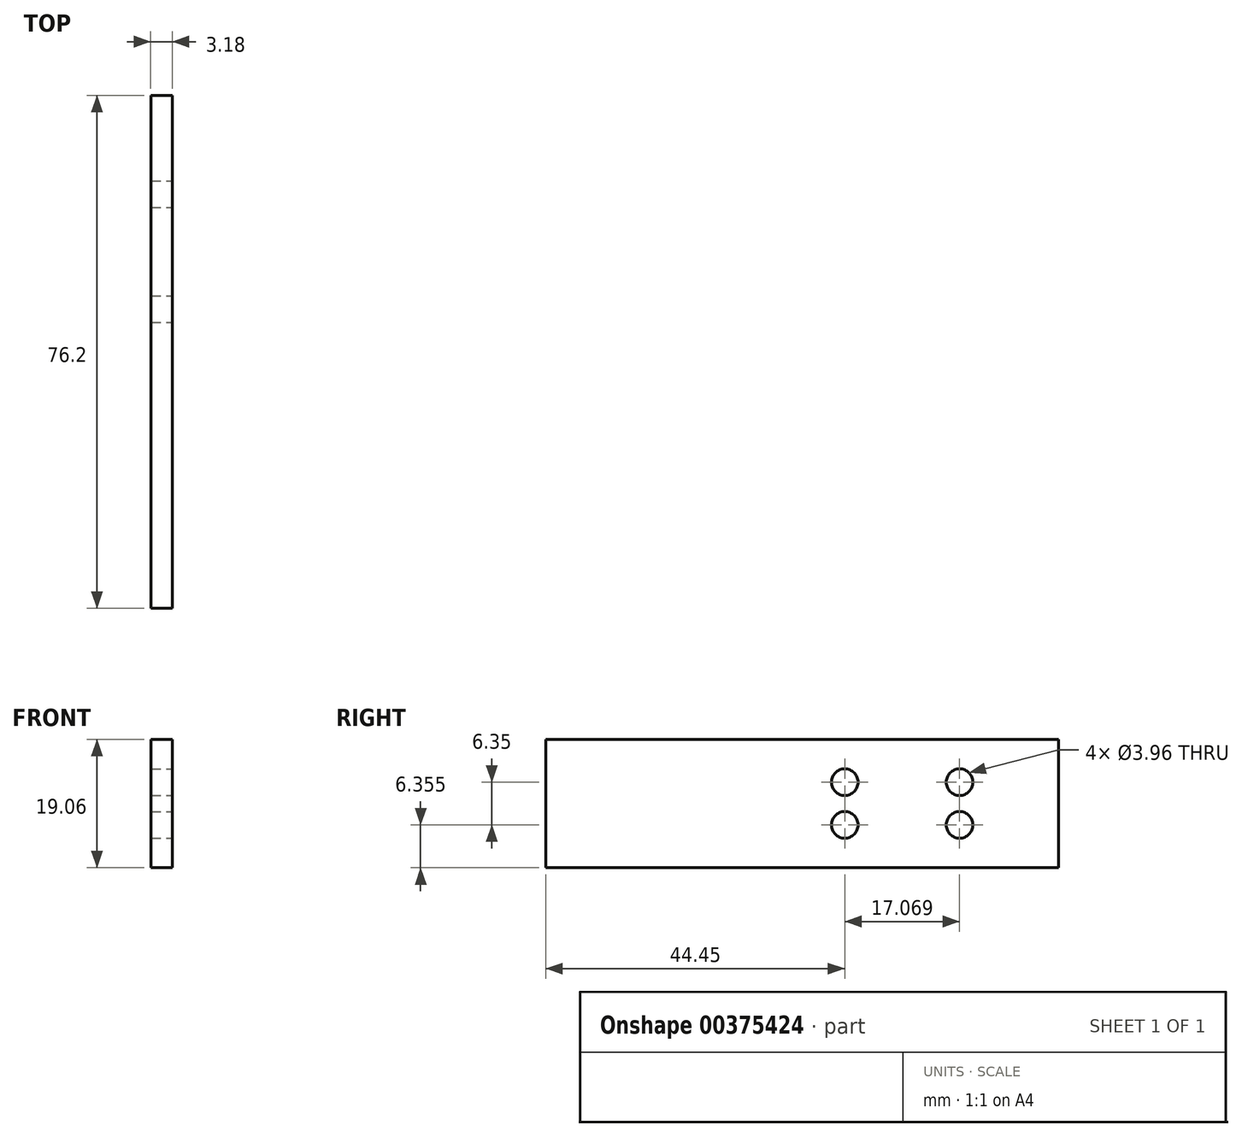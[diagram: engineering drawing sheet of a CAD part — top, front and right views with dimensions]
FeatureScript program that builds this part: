
annotation { "Feature Type Name" : "Feature", "Feature Type Description" : "" }
export const myFeature = defineFeature(function(context is Context, id is Id, definition is map)
    precondition{}
    {
        {
            var Q0;
            Q0=qCreatedBy(makeId("Front.planeOp"),FACE);
            var sketch = newSketch(context, id + "F0", { "sketchPlane" : qUnion([Q0])});
            skLineSegment(sketch, "E0.bottom", {"start": v(1.59, 9.52) * mm, "end": v(-1.59, 9.52) * mm});
            skLineSegment(sketch, "E0.top", {"start": v(1.59, -9.53) * mm, "end": v(-1.59, -9.53) * mm});
            skLineSegment(sketch, "E0.left", {"start": v(1.59, 9.52) * mm, "end": v(1.59, -9.53) * mm});
            skLineSegment(sketch, "E0.right", {"start": v(-1.59, 9.52) * mm, "end": v(-1.59, -9.53) * mm});
            skPoint(sketch, "E0.middle", {"position": v(0, 0) * mm});
            skSolve(sketch);
        }
        {
            var Q0;
            Q0=qSketchRegion(id+"F0",true);
            extrude(context, id + "F1", {"entities" : qUnion([Q0]), "depth" : 76.2 * mm, "symmetric" : true});
        }
        {
            var Q0;
            Q0=makeQuery(id+"F1.opExtrude","SWEPT_FACE",FACE,{"disambiguationData":[OSD([sQuery(id+"F0.wireOp",EDGE,"E0.left")])]});
            var sketch = newSketch(context, id + "F2", { "sketchPlane" : qUnion([Q0])});
            skCircle(sketch, "E1", {"center": v(23.42, 3.17) * mm, "radius": 1.98 * mm});
            skCircle(sketch, "E2", {"center": v(23.42, -3.17) * mm, "radius": 1.98 * mm});
            skSolve(sketch);
        }
        {
            var Q0;
            Q0=qSketchRegion(id+"F2",true);
            extrude(context, id + "F3", {"entities" : qUnion([Q0]), "operationType" : NewBodyOperationType.REMOVE, "endBound" : BoundingType.THROUGH_ALL, "oppositeDirection" : true, "depth" : 25.4 * mm});
        }
        {
            var Q0;
            Q0=makeQuery(id+"F1.opExtrude","SWEPT_FACE",FACE,{"disambiguationData":[OSD([sQuery(id+"F0.wireOp",EDGE,"E0.left")])]});
            var sketch = newSketch(context, id + "F4", { "sketchPlane" : qUnion([Q0])});
            skCircle(sketch, "E3", {"center": v(6.35, 3.17) * mm, "radius": 1.98 * mm});
            skCircle(sketch, "E4", {"center": v(6.35, -3.17) * mm, "radius": 1.98 * mm});
            skSolve(sketch);
        }
        {
            var Q0;
            Q0=qSketchRegion(id+"F4",true);
            extrude(context, id + "F5", {"entities" : qUnion([Q0]), "operationType" : NewBodyOperationType.REMOVE, "endBound" : BoundingType.THROUGH_ALL, "oppositeDirection" : true, "depth" : 25.4 * mm});
        }
    });
